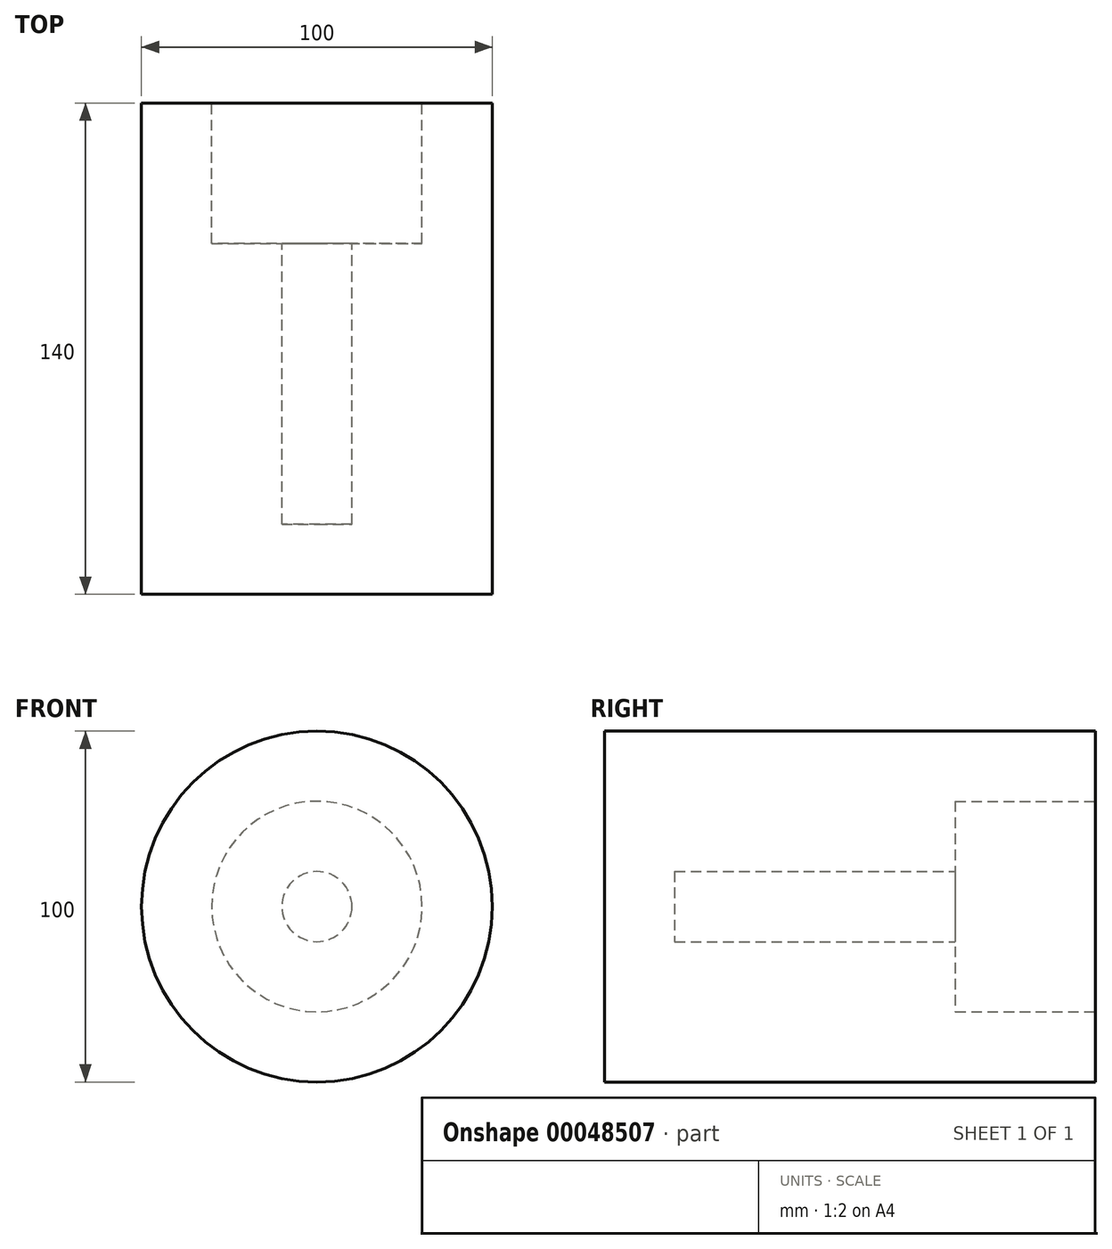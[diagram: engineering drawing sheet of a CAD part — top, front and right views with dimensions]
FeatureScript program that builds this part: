
annotation { "Feature Type Name" : "Feature", "Feature Type Description" : "" }
export const myFeature = defineFeature(function(context is Context, id is Id, definition is map)
    precondition{}
    {
        {
            var Q0;
            Q0=qCreatedBy(makeId("Right.planeOp"),FACE);
            var sketch = newSketch(context, id + "F0", { "sketchPlane" : qUnion([Q0])});
            skLineSegment(sketch, "E0", {"start": v(0, 0) * mm, "end": v(0, 50) * mm});
            skLineSegment(sketch, "E1", {"start": v(0, 50) * mm, "end": v(140, 50) * mm});
            skLineSegment(sketch, "E2", {"start": v(140, 50) * mm, "end": v(140, 0) * mm});
            skLineSegment(sketch, "E3", {"start": v(140, 0) * mm, "end": v(0, 0) * mm});
            skLineSegment(sketch, "E4", {"start": v(140, 30) * mm, "end": v(100, 30) * mm});
            skLineSegment(sketch, "E5", {"start": v(100, 30) * mm, "end": v(100, 10) * mm});
            skLineSegment(sketch, "E6", {"start": v(100, 10) * mm, "end": v(20, 10) * mm});
            skLineSegment(sketch, "E7", {"start": v(20, 10) * mm, "end": v(20, 0) * mm});
            skSolve(sketch);
        }
        {
            var Q0;
            {var subQ1=sQuery(id+"F0.wireOp",EDGE,"E0");Q0=makeQuery(id+"F0.imprint","IMPRINT",FACE,{"disambiguationData":[TD([[makeQuery(id+"F0.imprint","IMPRINT",EDGE,{"derivedFrom":subQ1}),-1.0]])]});}
            var Q1;
            Q1=sQuery(id+"F0.wireOp",EDGE,"E3");
            revolve(context, id + "F1", {"entities" : qUnion([Q0]), "axis" : qUnion([Q1]), "revolveType" : RevolveType.FULL});
        }
    });
